# Revit family: FU_Modular_Sandler_LIN 1050
name_source: partatom
category: Furniture
units: mm (PartAtom-declared; Revit-internal decimal feet)

## family parameters
Always vertical = Yes
Cut with Voids When Loaded = No
OmniClass Number = 23.40.20.00
OmniClass Title = General Furniture and Specialties
Room Calculation Point = No
Shared = No
Work Plane-Based = No

## types (1)
- Lin 1050
    Cross Support Number = 4
    Default Elevation = 0 mm  [stored 0 ft]
    Depth = 600 mm  [stored 1.9685 ft]
    Description = Structural frame with legs for 5 seater bench. Greenguard Certified.
    Height = 830 mm  [stored 2.7231 ft]
    Manufacturer = Sandler
    Model = Lin 1050
    Num Legs = 2
    URL = https://www.sandlerseating.com
    Width = 2960 mm  [stored 9.71129 ft]

note: [stored X ft] marks values corroborated as IEEE doubles in the binary element streams (Revit-internal decimal feet)

## geometry (parser evidence)
native form markers: Sweep x7
no freeform markers — native parametric forms only
